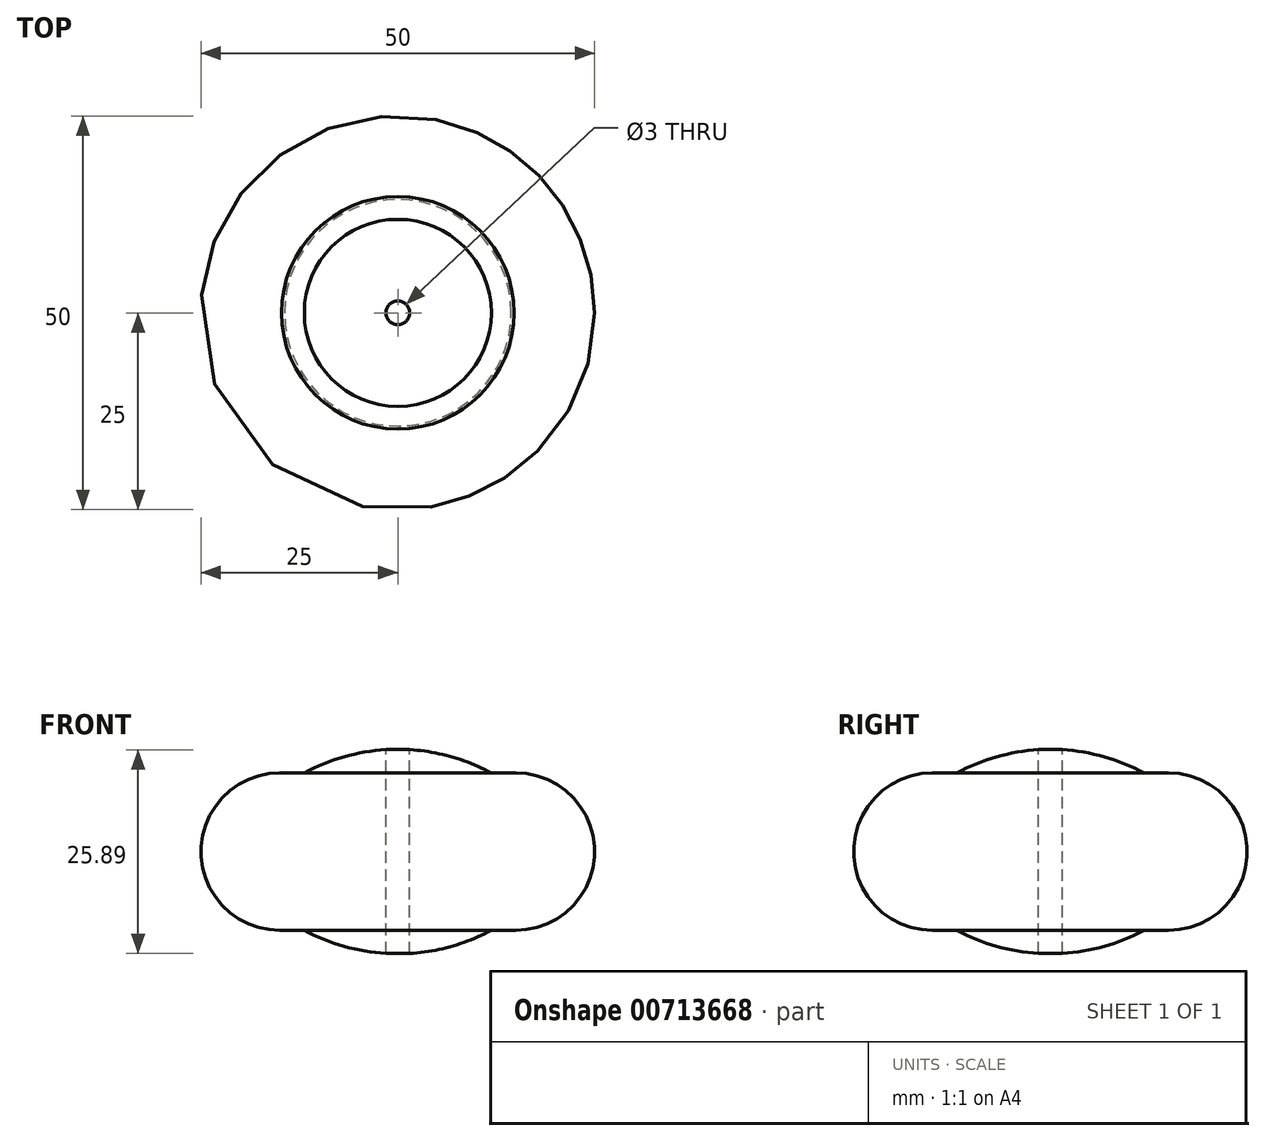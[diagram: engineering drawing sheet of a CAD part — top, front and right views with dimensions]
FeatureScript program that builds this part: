
annotation { "Feature Type Name" : "Feature", "Feature Type Description" : "" }
export const myFeature = defineFeature(function(context is Context, id is Id, definition is map)
    precondition{}
    {
        {
            var Q0;
            Q0=qCreatedBy(makeId("Front.planeOp"),FACE);
            var sketch = newSketch(context, id + "F0", { "sketchPlane" : qUnion([Q0])});
            skArc(sketch, "E0", {"start": v(-11.88, -9.98) * mm, "mid": v(-6.13, -12.22) * mm, "end": v(0, -12.99) * mm});
            skLineSegment(sketch, "E1", {"start": v(0, 0) * mm, "end": v(1105.39, 0) * mm, "construction": true});
            skLineSegment(sketch, "E2", {"start": v(0, 0) * mm, "end": v(0, 946.63) * mm, "construction": true});
            skArc(sketch, "E3", {"start": v(-14.77, 10) * mm, "mid": v(-25, -0.19) * mm, "end": v(-14.4, -9.98) * mm});
            skLineSegment(sketch, "E4", {"start": v(-14.77, 10) * mm, "end": v(-11.88, 10) * mm});
            skLineSegment(sketch, "E5", {"start": v(-15.62, -9.98) * mm, "end": v(-11.88, -9.98) * mm});
            skArc(sketch, "E6.trimOffspring", {"start": v(0, 13) * mm, "mid": v(-6.12, 12.24) * mm, "end": v(-11.88, 10) * mm});
            skLineSegment(sketch, "E7", {"start": v(0, 13) * mm, "end": v(0, -12.99) * mm});
            skPoint(sketch, "E8.center.orphan", {"position": v(15, 0) * mm});
            skSolve(sketch);
        }
        {
            var Q0;
            Q0 = qSketchRegion(id + "F0", true);
            var Q1;
            Q1=sQuery(id+"F0.wireOp",EDGE,"E7");
            revolve(context, id + "F1", {"surfaceOperationType" : NewSurfaceOperationType.NEW, "entities" : qUnion([Q0]), "axis" : qUnion([Q1]), "revolveType" : RevolveType.FULL});
        }
        {
            var Q0;
            Q0=qCreatedBy(makeId("Top.planeOp"),FACE);
            var sketch = newSketch(context, id + "F2", { "sketchPlane" : qUnion([Q0])});
            skCircle(sketch, "E9", {"center": v(0, 0) * mm, "radius": 1.5 * mm});
            skSolve(sketch);
        }
        {
            var Q0;
            Q0 = qSketchRegion(id + "F2", true);
            extrude(context, id + "F3", {"entities" : qUnion([Q0]), "operationType" : NewBodyOperationType.REMOVE, "endBound" : BoundingType.THROUGH_ALL, "oppositeDirection" : true, "depth" : 25.4 * mm, "offsetDistance" : 25.4 * mm, "hasSecondDirection" : true, "secondDirectionBound" : SecondDirectionBoundingType.THROUGH_ALL, "secondDirectionOppositeDirection" : false, "secondDirectionDepth" : 25.4 * mm});
        }
    });
